# Revit family: Скамья гардеробная
name_source: partatom
category: Оборудование
revit_build: Autodesk Revit 2017 (Build: 20170118_1100(x64)
units: mm (PartAtom-declared; Revit-internal decimal feet)

## family parameters
Всегда вертикально = Да
На основе рабочей плоскости = Нет
Общий = Нет
При загрузке вырезать с полостями = Нет
Размер круглого соединителя = Использовать диаметр
Тип детали = Нормальный
Точка расчета площади = Нет

## types (7) — shared parameters
Общ_Единицы измерения = шт.

## per-type parameters (varying)
| type | Группа модели | Общ_Высота | Общ_Глубина | Общ_Масса | Общ_Наименование | Общ_Ширина |
| 1000х400х400 | ТХ | 400 мм | 400 мм | 11,0 | Скамья гардеробная 1000х400х400 | 1000 мм |
| 600х385х460 | ТХ | 460 мм | 385 мм |  | Скамья гардеробная, 600х385х460 | 600 мм |
| 800х385х460 | ТХ | 460 мм | 385 мм |  | Скамья гардеробная, 800х385х460 | 800 мм |
| 1000х385х460 | ТХ | 460 мм | 385 мм |  | Скамья гардеробная, 1000х385х460 | 1000 мм |
| 1200х385х460 | ТХ | 460 мм | 385 мм |  | Скамья гардеробная, 1200х385х460 | 1200 мм |
| 1500х385х460 | ТХ | 460 мм | 385 мм |  | Скамья гардеробная, 1500х385х460 | 1500 мм |
| 2000х385х460 |  | 460 мм | 385 мм |  | Скамья гардеробная | 2000 мм |

## geometry (parser evidence)
native form markers: Blend x2
no freeform markers — native parametric forms only
